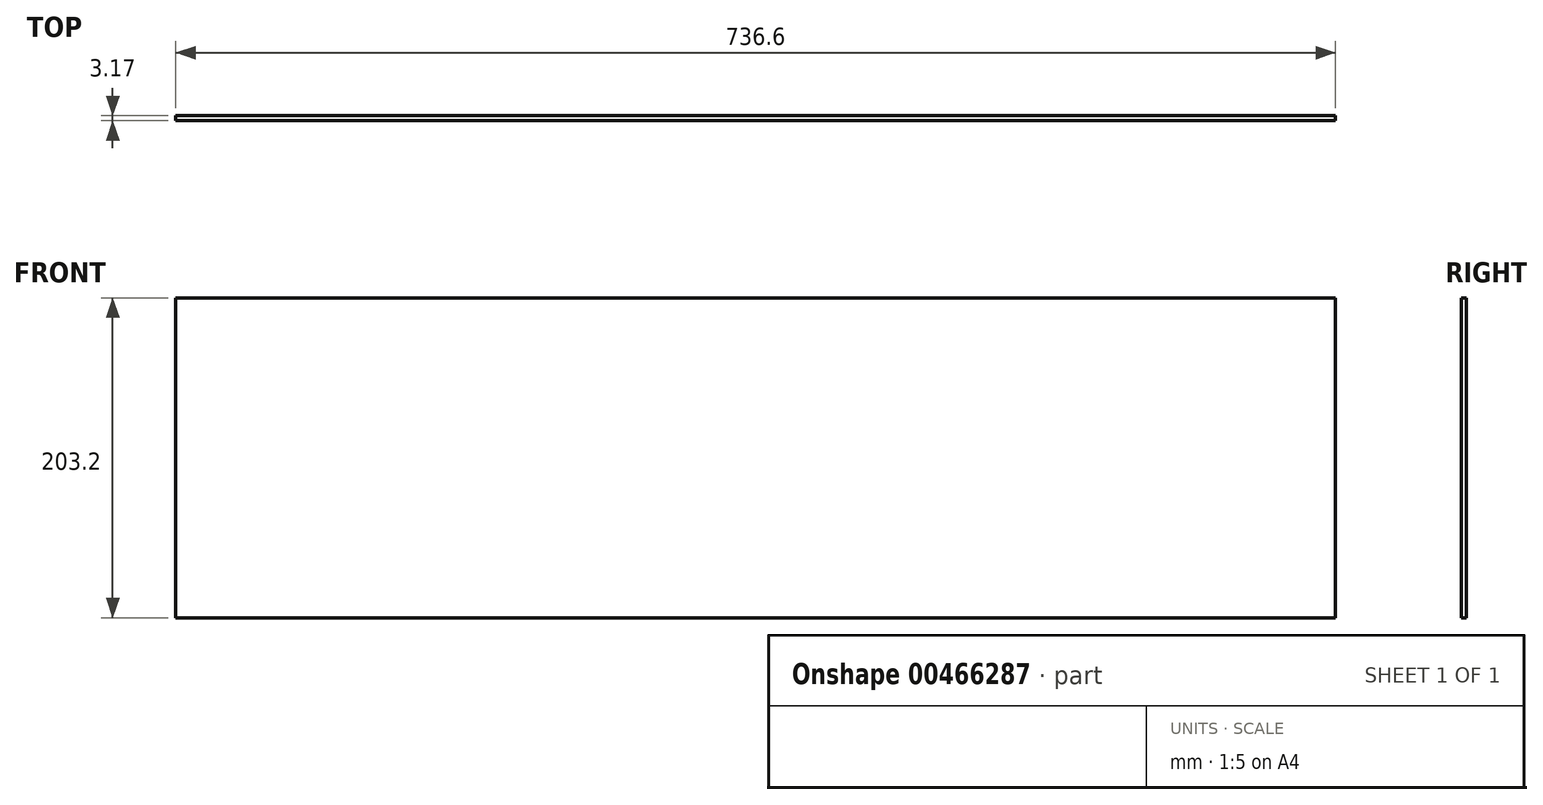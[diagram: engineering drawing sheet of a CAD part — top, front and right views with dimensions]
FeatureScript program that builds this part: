
annotation { "Feature Type Name" : "Feature", "Feature Type Description" : "" }
export const myFeature = defineFeature(function(context is Context, id is Id, definition is map)
    precondition{}
    {
        {
            var Q0;
            Q0=qCreatedBy(makeId("Front.planeOp"),FACE);
            var sketch = newSketch(context, id + "F0", { "sketchPlane" : qUnion([Q0])});
            skLineSegment(sketch, "E0", {"start": v(-367.72, 289.86) * mm, "end": v(368.88, 289.86) * mm});
            skLineSegment(sketch, "E1", {"start": v(368.88, 289.86) * mm, "end": v(368.88, 86.66) * mm});
            skLineSegment(sketch, "E2", {"start": v(368.88, 86.66) * mm, "end": v(-367.72, 86.66) * mm});
            skLineSegment(sketch, "E3", {"start": v(-367.72, 86.66) * mm, "end": v(-367.72, 289.86) * mm});
            skSolve(sketch);
        }
        {
            var Q0;
            Q0 = qSketchRegion(id + "F0", true);
            extrude(context, id + "F1", {"entities" : qUnion([Q0]), "depth" : 3.17 * mm, "offsetDistance" : 25.4 * mm});
        }
    });
